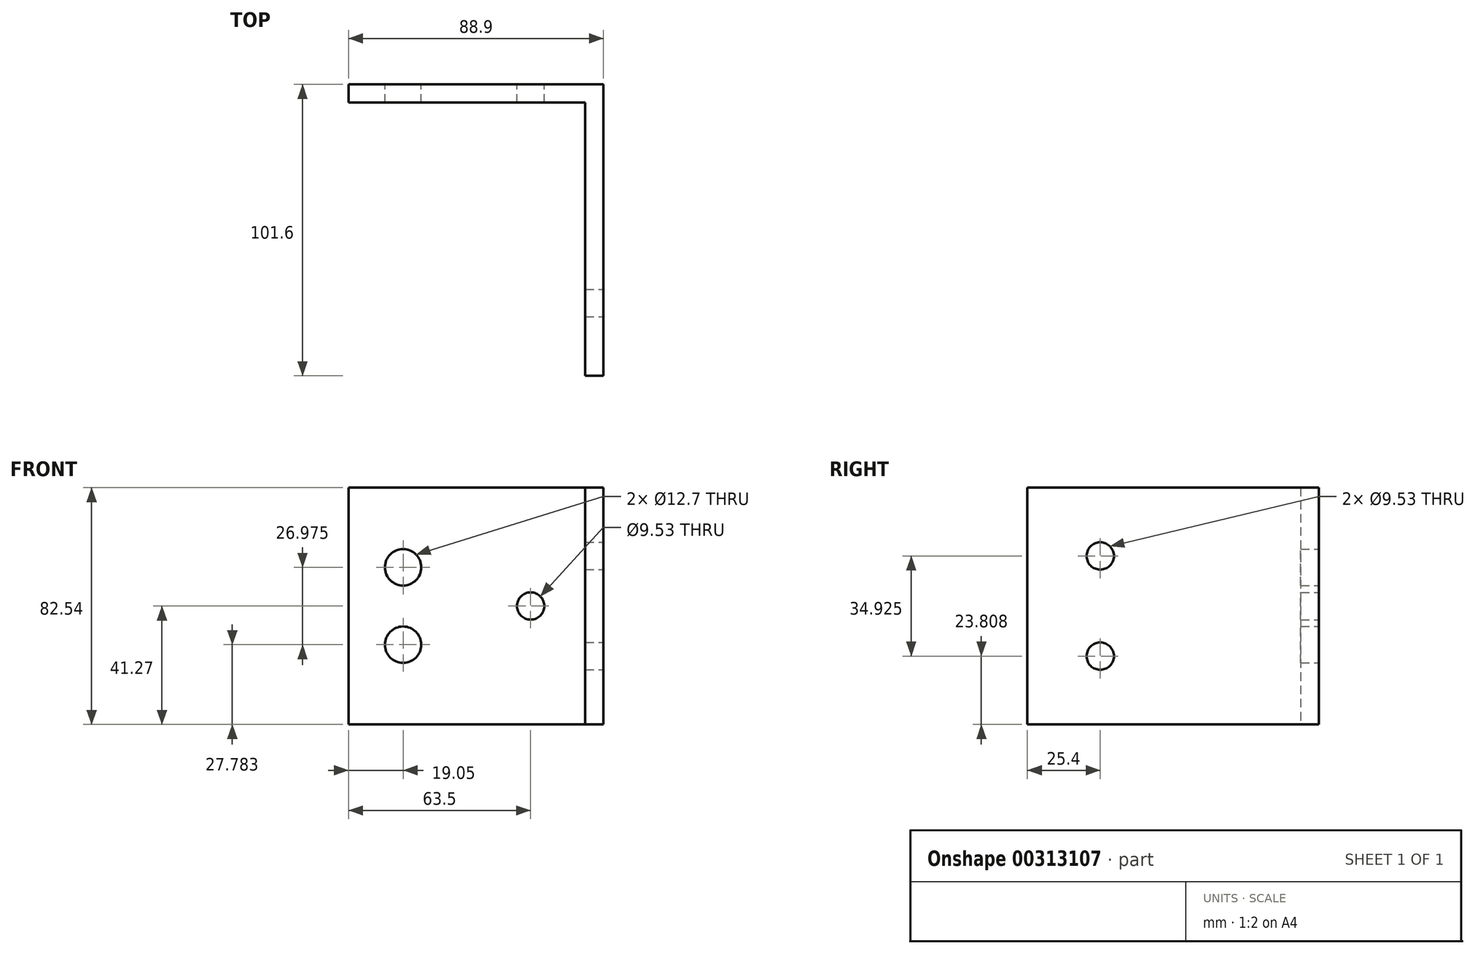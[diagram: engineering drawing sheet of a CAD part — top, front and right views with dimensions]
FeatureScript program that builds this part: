
annotation { "Feature Type Name" : "Feature", "Feature Type Description" : "" }
export const myFeature = defineFeature(function(context is Context, id is Id, definition is map)
    precondition{}
    {
        {
            var Q0;
            Q0=qCreatedBy(makeId("Top.planeOp"),FACE);
            var sketch = newSketch(context, id + "F0", { "sketchPlane" : qUnion([Q0])});
            skLineSegment(sketch, "E0", {"start": v(0, 0) * mm, "end": v(-82.55, 0) * mm});
            skLineSegment(sketch, "E1", {"start": v(-82.55, 0) * mm, "end": v(-82.55, 6.35) * mm});
            skLineSegment(sketch, "E2", {"start": v(-82.55, 6.35) * mm, "end": v(6.35, 6.35) * mm});
            skLineSegment(sketch, "E3", {"start": v(6.35, 6.35) * mm, "end": v(6.35, -95.25) * mm});
            skLineSegment(sketch, "E4", {"start": v(6.35, -95.25) * mm, "end": v(0, -95.25) * mm});
            skLineSegment(sketch, "E5", {"start": v(0, -95.25) * mm, "end": v(0, 0) * mm});
            skSolve(sketch);
        }
        {
            var Q0;
            Q0 = qSketchRegion(id + "F0", true);
            extrude(context, id + "F1", {"entities" : qUnion([Q0]), "endBound" : BoundingType.SYMMETRIC, "depth" : 82.55 * mm});
        }
        {
            var Q0;
            Q0=makeQuery(id+"F1.opExtrude","SWEPT_FACE",FACE,{"disambiguationData":[OSD([sQuery(id+"F0.wireOp",EDGE,"E3")])]});
            var sketch = newSketch(context, id + "F2", { "sketchPlane" : qUnion([Q0])});
            skCircle(sketch, "E6", {"center": v(-69.85, 17.46) * mm, "radius": 4.76 * mm});
            skCircle(sketch, "E7", {"center": v(-69.85, -17.46) * mm, "radius": 4.76 * mm});
            skLineSegment(sketch, "E8", {"start": v(-69.85, 17.46) * mm, "end": v(-69.85, -17.46) * mm, "construction": true});
            skPoint(sketch, "E9", {"position": v(-69.85, 0) * mm});
            skSolve(sketch);
        }
        {
            var Q0;
            Q0 = qSketchRegion(id + "F2", true);
            extrude(context, id + "F3", {"entities" : qUnion([Q0]), "operationType" : NewBodyOperationType.REMOVE, "endBound" : BoundingType.THROUGH_ALL, "oppositeDirection" : true, "depth" : 25.4 * mm});
        }
        {
            var Q0;
            Q0=makeQuery(id+"F1.opExtrude","SWEPT_FACE",FACE,{"disambiguationData":[OSD([sQuery(id+"F0.wireOp",EDGE,"E2")])]});
            var sketch = newSketch(context, id + "F4", { "sketchPlane" : qUnion([Q0])});
            skCircle(sketch, "E10", {"center": v(63.5, 13.49) * mm, "radius": 6.35 * mm});
            skCircle(sketch, "E11", {"center": v(63.5, -13.49) * mm, "radius": 6.35 * mm});
            skLineSegment(sketch, "E12", {"start": v(63.5, 13.49) * mm, "end": v(63.5, -13.49) * mm, "construction": true});
            skPoint(sketch, "E13", {"position": v(63.5, 0) * mm});
            skCircle(sketch, "E14", {"center": v(19.05, 0) * mm, "radius": 4.76 * mm});
            skSolve(sketch);
        }
        {
            var Q0;
            Q0 = qSketchRegion(id + "F4", true);
            extrude(context, id + "F5", {"entities" : qUnion([Q0]), "operationType" : NewBodyOperationType.REMOVE, "endBound" : BoundingType.THROUGH_ALL, "oppositeDirection" : true, "depth" : 25.4 * mm});
        }
    });
